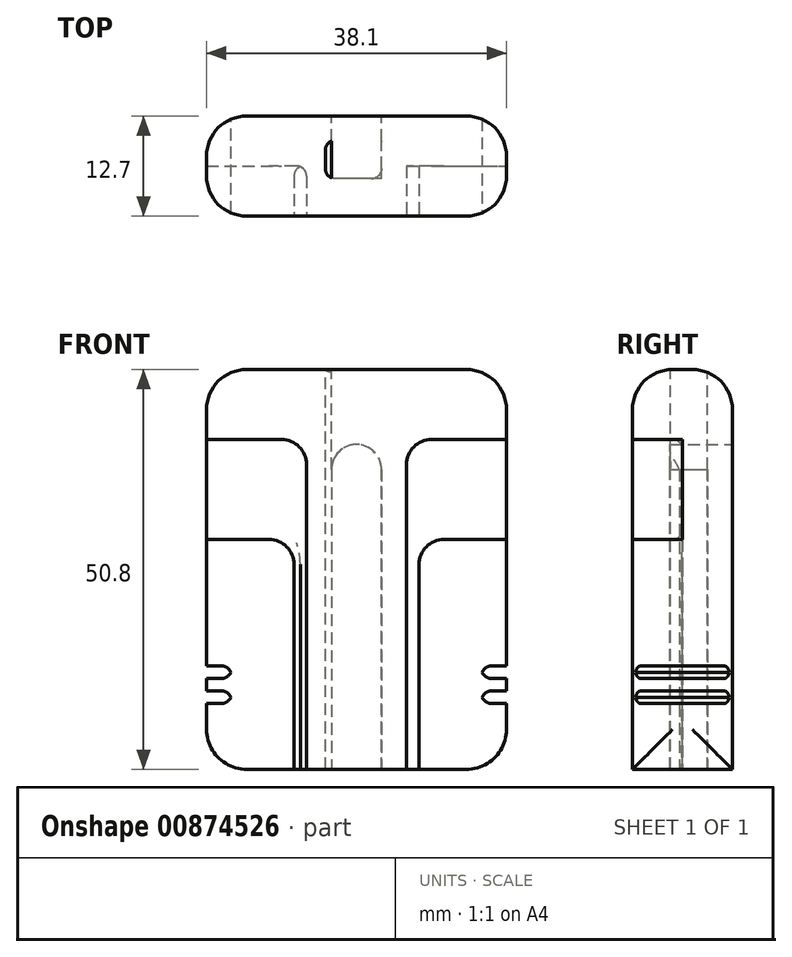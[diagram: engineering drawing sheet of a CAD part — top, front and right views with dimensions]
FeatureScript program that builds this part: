
annotation { "Feature Type Name" : "Feature", "Feature Type Description" : "" }
export const myFeature = defineFeature(function(context is Context, id is Id, definition is map)
    precondition{}
    {
        {
            var Q0;
            Q0=qCreatedBy(makeId("Front.planeOp"),FACE);
            var sketch = newSketch(context, id + "F0", { "sketchPlane" : qUnion([Q0])});
            skLineSegment(sketch, "E0.bottom", {"start": v(0, 50.8) * mm, "end": v(38.1, 50.8) * mm});
            skLineSegment(sketch, "E0.top", {"start": v(0, 0) * mm, "end": v(38.1, 0) * mm});
            skLineSegment(sketch, "E0.left", {"start": v(0, 50.8) * mm, "end": v(0, 0) * mm});
            skLineSegment(sketch, "E0.right", {"start": v(38.1, 50.8) * mm, "end": v(38.1, 0) * mm});
            skSolve(sketch);
        }
        {
            var Q0;
            Q0 = qSketchRegion(id + "F0", true);
            extrude(context, id + "F1", {"entities" : qUnion([Q0]), "depth" : 12.7 * mm, "offsetDistance" : 25.4 * mm});
        }
        {
            var Q0;
            Q0=makeQuery(id+"F1.opExtrude","CAP_FACE",FACE,{"disambiguationData":[OSD([sQuery(id+"F0.wireOp",EDGE,"E0.bottom"),sQuery(id+"F0.wireOp",EDGE,"E0.top"),sQuery(id+"F0.wireOp",EDGE,"E0.left"),sQuery(id+"F0.wireOp",EDGE,"E0.right")])],"isStart":false});
            var sketch = newSketch(context, id + "F2", { "sketchPlane" : qUnion([Q0])});
            skLineSegment(sketch, "E1.bottom", {"start": v(0, 41.91) * mm, "end": v(9.52, 41.91) * mm});
            skLineSegment(sketch, "E1.top", {"start": v(0, 29.21) * mm, "end": v(7.94, 29.21) * mm});
            skLineSegment(sketch, "E1.left", {"start": v(0, 41.91) * mm, "end": v(0, 29.21) * mm});
            skLineSegment(sketch, "E1.right", {"start": v(38.1, 41.91) * mm, "end": v(38.1, 29.21) * mm});
            skLineSegment(sketch, "E2.top", {"start": v(11.11, 0) * mm, "end": v(12.7, 0) * mm});
            skLineSegment(sketch, "E2.left", {"start": v(11.11, 26.04) * mm, "end": v(11.11, 0) * mm});
            skLineSegment(sketch, "E2.right", {"start": v(12.7, 29.21) * mm, "end": v(12.7, 0) * mm});
            skLineSegment(sketch, "E3.top", {"start": v(25.4, 0) * mm, "end": v(26.99, 0) * mm});
            skLineSegment(sketch, "E3.left", {"start": v(25.4, 29.2) * mm, "end": v(25.4, 0) * mm});
            skLineSegment(sketch, "E3.right", {"start": v(26.99, 26.03) * mm, "end": v(26.99, 0) * mm});
            skLineSegment(sketch, "E4.left", {"start": v(12.7, 29.21) * mm, "end": v(12.7, 38.74) * mm});
            skLineSegment(sketch, "E4.right", {"start": v(25.4, 29.24) * mm, "end": v(25.4, 38.73) * mm});
            skLineSegment(sketch, "E5.trimOffspring", {"start": v(30.16, 29.21) * mm, "end": v(38.1, 29.21) * mm});
            skLineSegment(sketch, "E6.trimOffspring", {"start": v(28.58, 41.91) * mm, "end": v(38.1, 41.91) * mm});
            skPoint(sketch, "E7.visualSharp", {"position": v(11.11, 29.21) * mm});
            skArc(sketch, "E7.filletArc", {"start": v(11.11, 26.04) * mm, "mid": v(10.18, 28.28) * mm, "end": v(7.94, 29.21) * mm});
            skPoint(sketch, "E8.visualSharp", {"position": v(12.7, 41.91) * mm});
            skArc(sketch, "E8.filletArc", {"start": v(12.7, 38.74) * mm, "mid": v(11.77, 40.98) * mm, "end": v(9.52, 41.91) * mm});
            skPoint(sketch, "E9.visualSharp", {"position": v(25.4, 41.9) * mm});
            skArc(sketch, "E9.filletArc", {"start": v(28.58, 41.9) * mm, "mid": v(26.33, 40.98) * mm, "end": v(25.4, 38.73) * mm});
            skPoint(sketch, "E10.visualSharp", {"position": v(26.99, 29.2) * mm});
            skArc(sketch, "E10.filletArc", {"start": v(30.16, 29.2) * mm, "mid": v(27.92, 28.28) * mm, "end": v(26.99, 26.03) * mm});
            skLineSegment(sketch, "E11.bottom", {"start": v(0, 9.97) * mm, "end": v(3.18, 9.97) * mm});
            skLineSegment(sketch, "E11.top", {"start": v(0, 8.38) * mm, "end": v(3.18, 8.38) * mm});
            skLineSegment(sketch, "E11.left", {"start": v(0, 9.97) * mm, "end": v(0, 8.38) * mm});
            skLineSegment(sketch, "E11.right", {"start": v(3.18, 9.97) * mm, "end": v(3.18, 8.38) * mm});
            skLineSegment(sketch, "E12.bottom", {"start": v(38.1, 9.97) * mm, "end": v(34.93, 9.97) * mm});
            skLineSegment(sketch, "E12.top", {"start": v(38.1, 8.38) * mm, "end": v(34.93, 8.38) * mm});
            skLineSegment(sketch, "E12.left", {"start": v(38.1, 9.97) * mm, "end": v(38.1, 8.38) * mm});
            skLineSegment(sketch, "E12.right", {"start": v(34.93, 9.97) * mm, "end": v(34.93, 8.38) * mm});
            skLineSegment(sketch, "E13", {"start": v(19.05, 0) * mm, "end": v(19.05, 50.8) * mm});
            skArc(sketch, "E14.MirrorCS", {"start": v(25.4, 38.74) * mm, "mid": v(26.33, 40.98) * mm, "end": v(28.58, 41.91) * mm});
            skLineSegment(sketch, "E15.MirrorCS", {"start": v(38.1, 41.91) * mm, "end": v(28.58, 41.91) * mm});
            skLineSegment(sketch, "E16.MirrorCS", {"start": v(38.1, 29.21) * mm, "end": v(30.16, 29.21) * mm});
            skArc(sketch, "E17.MirrorCS", {"start": v(26.99, 26.04) * mm, "mid": v(27.92, 28.28) * mm, "end": v(30.16, 29.21) * mm});
            skLineSegment(sketch, "E18.MirrorCS", {"start": v(26.99, 26.04) * mm, "end": v(26.99, 0) * mm});
            skLineSegment(sketch, "E19.MirrorCS", {"start": v(25.4, 29.21) * mm, "end": v(25.4, 0) * mm});
            skLineSegment(sketch, "E20.MirrorCS", {"start": v(25.4, 29.21) * mm, "end": v(25.4, 38.74) * mm});
            skLineSegment(sketch, "E21.bottom", {"start": v(3.18, 9.97) * mm, "end": v(0, 9.97) * mm});
            skLineSegment(sketch, "E21.top", {"start": v(3.18, 10.76) * mm, "end": v(0, 10.76) * mm});
            skLineSegment(sketch, "E21.left", {"start": v(3.18, 9.97) * mm, "end": v(3.18, 10.76) * mm});
            skLineSegment(sketch, "E21.right", {"start": v(0, 9.97) * mm, "end": v(0, 10.76) * mm});
            skLineSegment(sketch, "E22.bottom", {"start": v(34.93, 9.97) * mm, "end": v(38.1, 9.97) * mm});
            skLineSegment(sketch, "E22.top", {"start": v(34.93, 10.76) * mm, "end": v(38.1, 10.76) * mm});
            skLineSegment(sketch, "E22.left", {"start": v(34.93, 9.97) * mm, "end": v(34.93, 10.76) * mm});
            skLineSegment(sketch, "E22.right", {"start": v(38.1, 9.97) * mm, "end": v(38.1, 10.76) * mm});
            skLineSegment(sketch, "E23.MirrorCS", {"start": v(3.18, 11.56) * mm, "end": v(3.18, 13.14) * mm});
            skLineSegment(sketch, "E24.MirrorCS", {"start": v(0, 11.56) * mm, "end": v(3.18, 11.56) * mm});
            skLineSegment(sketch, "E25.MirrorCS", {"start": v(0, 13.14) * mm, "end": v(3.18, 13.14) * mm});
            skLineSegment(sketch, "E26.MirrorCS", {"start": v(34.93, 11.56) * mm, "end": v(34.93, 13.14) * mm});
            skLineSegment(sketch, "E27.MirrorCS", {"start": v(38.1, 13.14) * mm, "end": v(34.93, 13.14) * mm});
            skLineSegment(sketch, "E28.MirrorCS", {"start": v(38.1, 11.56) * mm, "end": v(34.93, 11.56) * mm});
            skSolve(sketch);
        }
        {
            var Q0;
            Q0=makeQuery(id+"F2.imprint","IMPRINT",FACE,{"disambiguationData":[TD([[makeQuery(id+"F2.imprint","IMPRINT",EDGE,{"derivedFrom":sQuery(id+"F2.wireOp",EDGE,"E1.bottom")}),-1.0]])]});
            var Q1;
            Q1=makeQuery(id+"F2.imprint","IMPRINT",FACE,{"disambiguationData":[TD([[makeQuery(id+"F2.imprint","IMPRINT",EDGE,{"derivedFrom":sQuery(id+"F2.wireOp",EDGE,"E1.right")}),-1.0]])]});
            extrude(context, id + "F3", {"entities" : qUnion([Q0, Q1]), "operationType" : NewBodyOperationType.REMOVE, "oppositeDirection" : true, "depth" : 6.35 * mm, "offsetDistance" : 25.4 * mm});
        }
        {
            var Q0;
            Q0=makeQuery(id+"F2.imprint","IMPRINT",FACE,{"disambiguationData":[TD([[makeQuery(id+"F2.imprint","IMPRINT",EDGE,{"derivedFrom":sQuery(id+"F2.wireOp",EDGE,"E23.MirrorCS")}),1.0]])]});
            var Q1;
            Q1=makeQuery(id+"F2.imprint","IMPRINT",FACE,{"disambiguationData":[TD([[makeQuery(id+"F2.imprint","IMPRINT",EDGE,{"derivedFrom":sQuery(id+"F2.wireOp",EDGE,"E26.MirrorCS")}),-1.0]])]});
            var Q2;
            Q2=makeQuery(id+"F2.imprint","IMPRINT",FACE,{"disambiguationData":[TD([[makeQuery(id+"F2.imprint","IMPRINT",EDGE,{"derivedFrom":sQuery(id+"F2.wireOp",EDGE,"E12.top")}),-1.0]])]});
            var Q3;
            Q3=makeQuery(id+"F2.imprint","IMPRINT",FACE,{"disambiguationData":[TD([[makeQuery(id+"F2.imprint","IMPRINT",EDGE,{"derivedFrom":sQuery(id+"F2.wireOp",EDGE,"E11.top")}),1.0]])]});
            extrude(context, id + "F4", {"entities" : qUnion([Q0, Q1, Q2, Q3]), "operationType" : NewBodyOperationType.REMOVE, "endBound" : BoundingType.THROUGH_ALL, "oppositeDirection" : true, "depth" : 6.35 * mm, "offsetDistance" : 25.4 * mm});
        }
        {
            var Q0;
            Q0=makeQuery(id+"F2.imprint","IMPRINT",FACE,{"disambiguationData":[TD([[makeQuery(id+"F2.imprint","IMPRINT",EDGE,{"derivedFrom":sQuery(id+"F2.wireOp",EDGE,"E1.right")}),-1.0]])]});
            extrude(context, id + "F5", {"entities" : qUnion([Q0]), "operationType" : NewBodyOperationType.REMOVE, "oppositeDirection" : true, "depth" : 6.35 * mm, "offsetDistance" : 25.4 * mm});
        }
        {
            var Q0;
            Q0=makeQuery(id+"F3.boolean.opBoolean","COPY",EDGE,{"derivedFrom":makeQuery(id+"F3.opExtrude","CAP_EDGE",EDGE,{"disambiguationData":[OSD([sQuery(id+"F2.wireOp",EDGE,"E1.bottom")])],"isStart":false})});
            var Q1;
            Q1=makeQuery(id+"F3.boolean.opBoolean","COPY",EDGE,{"derivedFrom":makeQuery(id+"F3.opExtrude","CAP_EDGE",EDGE,{"disambiguationData":[OSD([sQuery(id+"F2.wireOp",EDGE,"E15.MirrorCS")])],"isStart":false})});
            var Q2;
            Q2=makeQuery(id+"F3.boolean.opBoolean","COPY",EDGE,{"derivedFrom":makeQuery(id+"F3.opExtrude","CAP_EDGE",EDGE,{"disambiguationData":[OSD([sQuery(id+"F2.wireOp",EDGE,"E16.MirrorCS")])],"isStart":false})});
            var Q3;
            Q3=makeQuery(id+"F3.boolean.opBoolean","COPY",EDGE,{"derivedFrom":makeQuery(id+"F3.opExtrude","CAP_EDGE",EDGE,{"disambiguationData":[OSD([sQuery(id+"F2.wireOp",EDGE,"E1.top")])],"isStart":false})});
            var Q4;
            Q4=makeQuery(id+"F4.boolean.opBoolean","COPY",EDGE,{"derivedFrom":makeQuery(id+"F4.opExtrude","SWEPT_EDGE",EDGE,{"disambiguationData":[OSD([sQuery(id+"F2.wireOp",EDGE,"E26.MirrorCS"),sQuery(id+"F2.wireOp",EDGE,"E28.MirrorCS")])]})});
            var Q5;
            Q5=makeQuery(id+"F4.boolean.opBoolean","COPY",EDGE,{"derivedFrom":makeQuery(id+"F4.opExtrude","SWEPT_EDGE",EDGE,{"disambiguationData":[OSD([sQuery(id+"F2.wireOp",EDGE,"E12.top"),sQuery(id+"F2.wireOp",EDGE,"E12.right")])]})});
            var Q6;
            Q6=makeQuery(id+"F4.boolean.opBoolean","COPY",EDGE,{"derivedFrom":makeQuery(id+"F4.opExtrude","SWEPT_EDGE",EDGE,{"disambiguationData":[OSD([sQuery(id+"F2.wireOp",EDGE,"E26.MirrorCS"),sQuery(id+"F2.wireOp",EDGE,"E27.MirrorCS")])]})});
            var Q7;
            Q7=makeQuery(id+"F4.boolean.opBoolean","COPY",EDGE,{"derivedFrom":makeQuery(id+"F4.opExtrude","SWEPT_EDGE",EDGE,{"disambiguationData":[OSD([sQuery(id+"F2.wireOp",EDGE,"E12.right"),sQuery(id+"F2.wireOp",EDGE,"E22.bottom"),sQuery(id+"F2.wireOp",EDGE,"E22.left")])]})});
            var Q8;
            Q8=makeQuery(id+"F4.boolean.opBoolean","COPY",EDGE,{"derivedFrom":makeQuery(id+"F4.opExtrude","SWEPT_EDGE",EDGE,{"disambiguationData":[OSD([sQuery(id+"F2.wireOp",EDGE,"E11.top"),sQuery(id+"F2.wireOp",EDGE,"E11.right")])]})});
            var Q9;
            Q9=makeQuery(id+"F4.boolean.opBoolean","COPY",EDGE,{"derivedFrom":makeQuery(id+"F4.opExtrude","SWEPT_EDGE",EDGE,{"disambiguationData":[OSD([sQuery(id+"F2.wireOp",EDGE,"E23.MirrorCS"),sQuery(id+"F2.wireOp",EDGE,"E24.MirrorCS")])]})});
            var Q10;
            Q10=makeQuery(id+"F4.boolean.opBoolean","COPY",EDGE,{"derivedFrom":makeQuery(id+"F4.opExtrude","SWEPT_EDGE",EDGE,{"disambiguationData":[OSD([sQuery(id+"F2.wireOp",EDGE,"E11.right"),sQuery(id+"F2.wireOp",EDGE,"E21.bottom"),sQuery(id+"F2.wireOp",EDGE,"E21.left")])]})});
            var Q11;
            Q11=makeQuery(id+"F4.boolean.opBoolean","COPY",EDGE,{"derivedFrom":makeQuery(id+"F4.opExtrude","SWEPT_EDGE",EDGE,{"disambiguationData":[OSD([sQuery(id+"F2.wireOp",EDGE,"E23.MirrorCS"),sQuery(id+"F2.wireOp",EDGE,"E25.MirrorCS")])]})});
            fillet(context, id + "F6", {"entities" : qUnion([Q0, Q1, Q2, Q3, Q4, Q5, Q6, Q7, Q8, Q9, Q10, Q11]), "radius" : 1.27 * mm, "tangentPropagation" : true, "allowEdgeOverflow" : false});
        }
        {
            var Q0;
            Q0=qCreatedBy(makeId("Front.planeOp"),FACE);
            var sketch = newSketch(context, id + "F7", { "sketchPlane" : qUnion([Q0])});
            skLineSegment(sketch, "E29.bottom", {"start": v(19.05, 41.28) * mm, "end": v(19.05, 41.28) * mm});
            skLineSegment(sketch, "E29.top", {"start": v(22.23, 0) * mm, "end": v(15.88, 0) * mm});
            skLineSegment(sketch, "E29.left", {"start": v(22.23, 38.1) * mm, "end": v(22.22, 0) * mm});
            skLineSegment(sketch, "E29.right", {"start": v(15.88, 38.1) * mm, "end": v(15.88, 0) * mm});
            skPoint(sketch, "E30", {"position": v(19.05, 0) * mm});
            skPoint(sketch, "E31.visualSharp", {"position": v(15.88, 41.28) * mm});
            skArc(sketch, "E31.filletArc", {"start": v(19.05, 41.28) * mm, "mid": v(16.8, 40.35) * mm, "end": v(15.88, 38.1) * mm});
            skLineSegment(sketch, "E32.0", {"start": v(15.08, 38.1) * mm, "end": v(15.08, 0) * mm});
            skPoint(sketch, "E33.visualSharp", {"position": v(22.23, 41.28) * mm});
            skArc(sketch, "E33.filletArc", {"start": v(22.23, 38.1) * mm, "mid": v(21.3, 40.35) * mm, "end": v(19.05, 41.28) * mm});
            skLineSegment(sketch, "E34.0", {"start": v(23.02, 38.1) * mm, "end": v(23.02, 0) * mm});
            skArc(sketch, "E35.0", {"start": v(19.05, 42.07) * mm, "mid": v(16.24, 40.9) * mm, "end": v(15.08, 38.1) * mm});
            skArc(sketch, "E35.1", {"start": v(23.02, 38.1) * mm, "mid": v(21.86, 40.9) * mm, "end": v(19.05, 42.07) * mm});
            skSolve(sketch);
        }
        {
            var Q0;
            Q0=makeQuery(id+"F7.imprint","IMPRINT",FACE,{"disambiguationData":[TD([[makeQuery(id+"F7.imprint","IMPRINT",EDGE,{"derivedFrom":sQuery(id+"F7.wireOp",EDGE,"E29.top")}),-1.0]])]});
            extrude(context, id + "F8", {"entities" : qUnion([Q0]), "operationType" : NewBodyOperationType.REMOVE, "depth" : 7.94 * mm, "offsetDistance" : 25.4 * mm});
        }
        {
            var Q0;
            Q0=makeQuery(id+"F8.boolean.opBoolean","COPY",FACE,{"derivedFrom":makeQuery(id+"F8.opExtrude","SWEPT_FACE",FACE,{"disambiguationData":[OSD([sQuery(id+"F7.wireOp",EDGE,"E29.left")])]})});
            var sketch = newSketch(context, id + "F9", { "sketchPlane" : qUnion([Q0])});
            skLineSegment(sketch, "E36.bottom", {"start": v(7.94, 38.1) * mm, "end": v(3.18, 38.1) * mm});
            skLineSegment(sketch, "E36.top", {"start": v(7.94, 0) * mm, "end": v(3.18, 0) * mm});
            skLineSegment(sketch, "E36.left", {"start": v(7.94, 38.1) * mm, "end": v(7.94, 0) * mm});
            skLineSegment(sketch, "E36.right", {"start": v(3.17, 38.1) * mm, "end": v(3.18, 0) * mm});
            skSolve(sketch);
        }
        {
            var Q0;
            Q0 = qSketchRegion(id + "F9", true);
            extrude(context, id + "F10", {"entities" : qUnion([Q0]), "operationType" : NewBodyOperationType.REMOVE, "oppositeDirection" : true, "depth" : 1 / 812.8 * mm, "offsetDistance" : 25.4 * mm});
        }
        {
            var Q0;
            Q0=makeQuery(id+"F8.boolean.opBoolean","COPY",FACE,{"derivedFrom":makeQuery(id+"F8.opExtrude","SWEPT_FACE",FACE,{"disambiguationData":[OSD([sQuery(id+"F7.wireOp",EDGE,"E29.right")])]})});
            var sketch = newSketch(context, id + "F11", { "sketchPlane" : qUnion([Q0])});
            skLineSegment(sketch, "E37.bottom", {"start": v(-7.94, 0) * mm, "end": v(-3.17, 0) * mm});
            skLineSegment(sketch, "E37.top", {"start": v(-7.94, 57.15) * mm, "end": v(-3.18, 57.15) * mm});
            skLineSegment(sketch, "E37.left", {"start": v(-7.94, 0) * mm, "end": v(-7.94, 57.15) * mm});
            skLineSegment(sketch, "E37.right", {"start": v(-3.17, 0) * mm, "end": v(-3.18, 57.15) * mm});
            skSolve(sketch);
        }
        {
            var Q0;
            Q0 = qSketchRegion(id + "F11", true);
            extrude(context, id + "F12", {"entities" : qUnion([Q0]), "operationType" : NewBodyOperationType.REMOVE, "oppositeDirection" : true, "depth" : 0.8 * mm, "offsetDistance" : 25.4 * mm});
        }
        {
            var Q0;
            Q0=makeQuery(id+"F10.boolean.opBoolean","COPY",EDGE,{"derivedFrom":makeQuery(id+"F10.opExtrude","CAP_EDGE",EDGE,{"disambiguationData":[OSD([sQuery(id+"F9.wireOp",EDGE,"E36.left")])],"isStart":false})});
            var Q1;
            Q1=makeQuery(id+"F12.boolean.opBoolean","COPY",EDGE,{"derivedFrom":makeQuery(id+"F12.opExtrude","CAP_EDGE",EDGE,{"disambiguationData":[OSD([sQuery(id+"F11.wireOp",EDGE,"E37.left")])],"isStart":false})});
            var Q2;
            Q2=makeQuery(id+"F12.boolean.opBoolean","COPY",EDGE,{"derivedFrom":makeQuery(id+"F12.opExtrude","CAP_EDGE",EDGE,{"disambiguationData":[OSD([sQuery(id+"F11.wireOp",EDGE,"E37.right")])],"isStart":false})});
            var Q3;
            Q3=makeQuery(id+"F10.boolean.opBoolean","COPY",EDGE,{"derivedFrom":makeQuery(id+"F10.opExtrude","CAP_EDGE",EDGE,{"disambiguationData":[OSD([sQuery(id+"F9.wireOp",EDGE,"E36.right")])],"isStart":false})});
            var Q4;
            Q4=makeQuery(id+"F8.boolean.opBoolean","COPY",EDGE,{"derivedFrom":makeQuery(id+"F8.opExtrude","CAP_EDGE",EDGE,{"disambiguationData":[OSD([sQuery(id+"F7.wireOp",EDGE,"E29.left")])],"isStart":true})});
            fillet(context, id + "F13", {"entities" : qUnion([Q0, Q1, Q2, Q3, Q4]), "radius" : 1.27 * mm, "tangentPropagation" : true, "allowEdgeOverflow" : false});
        }
        {
            var Q0;
            {var subQ0=sQuery(id+"F0.wireOp",EDGE,"E0.bottom");var subQ1=sQuery(id+"F0.wireOp",EDGE,"E0.right");Q0=makeQuery(id+"F3.boolean.opBoolean","SPLIT",EDGE,{"disambiguationData":[TD([makeQuery(id+"F1.opExtrude","SWEPT_FACE",FACE,{"disambiguationData":[OSD([subQ0])]})])],"derivedFrom":makeQuery(id+"F1.opExtrude","CAP_EDGE",EDGE,{"disambiguationData":[OSD([subQ1])],"isStart":true})});}
            var Q1;
            Q1=makeQuery(id+"F1.opExtrude","CAP_EDGE",EDGE,{"disambiguationData":[OSD([sQuery(id+"F0.wireOp",EDGE,"E0.bottom")])],"isStart":true});
            var Q2;
            {var subQ0=sQuery(id+"F0.wireOp",EDGE,"E0.bottom");var subQ1=sQuery(id+"F0.wireOp",EDGE,"E0.left");Q2=makeQuery(id+"F3.boolean.opBoolean","SPLIT",EDGE,{"disambiguationData":[TD([makeQuery(id+"F1.opExtrude","SWEPT_FACE",FACE,{"disambiguationData":[OSD([subQ0])]})])],"derivedFrom":makeQuery(id+"F1.opExtrude","CAP_EDGE",EDGE,{"disambiguationData":[OSD([subQ1])],"isStart":true})});}
            var Q3;
            {var subQ0=sQuery(id+"F0.wireOp",EDGE,"E0.right");var subQ1=sQuery(id+"F0.wireOp",EDGE,"E0.top");Q3=makeQuery(id+"F3.boolean.opBoolean","SPLIT",EDGE,{"disambiguationData":[TD([makeQuery(id+"F1.opExtrude","SWEPT_FACE",FACE,{"disambiguationData":[OSD([subQ1])]})])],"derivedFrom":makeQuery(id+"F1.opExtrude","CAP_EDGE",EDGE,{"disambiguationData":[OSD([subQ0])],"isStart":true})});}
            var Q4;
            Q4=makeQuery(id+"F1.opExtrude","CAP_EDGE",EDGE,{"disambiguationData":[OSD([sQuery(id+"F0.wireOp",EDGE,"E0.bottom")])],"isStart":false});
            var Q5;
            {var subQ0=sQuery(id+"F0.wireOp",EDGE,"E0.right");var subQ1=sQuery(id+"F0.wireOp",EDGE,"E0.bottom");var subQ3=makeQuery(id+"F3.opExtrude","SWEPT_FACE",FACE,{"disambiguationData":[OSD([sQuery(id+"F2.wireOp",EDGE,"E12.bottom")])]});Q5=makeQuery(id+"F5.boolean.opBoolean","SPLIT",EDGE,{"disambiguationData":[TD([makeQuery(id+"F3.boolean.opBoolean","COPY",FACE,{"derivedFrom":subQ3})])],"derivedFrom":makeQuery(id+"F3.boolean.opBoolean","SPLIT",EDGE,{"disambiguationData":[TD([makeQuery(id+"F1.opExtrude","SWEPT_FACE",FACE,{"disambiguationData":[OSD([subQ1])]})])],"derivedFrom":makeQuery(id+"F1.opExtrude","CAP_EDGE",EDGE,{"disambiguationData":[OSD([subQ0])],"isStart":false})})});}
            var Q6;
            {var subQ0=sQuery(id+"F0.wireOp",EDGE,"E0.right");var subQ1=sQuery(id+"F0.wireOp",EDGE,"E0.top");Q6=makeQuery(id+"F3.boolean.opBoolean","SPLIT",EDGE,{"disambiguationData":[TD([makeQuery(id+"F1.opExtrude","SWEPT_FACE",FACE,{"disambiguationData":[OSD([subQ1])]})])],"derivedFrom":makeQuery(id+"F1.opExtrude","CAP_EDGE",EDGE,{"disambiguationData":[OSD([subQ0])],"isStart":false})});}
            var Q7;
            {var subQ0=sQuery(id+"F0.wireOp",EDGE,"E0.left");var subQ1=sQuery(id+"F0.wireOp",EDGE,"E0.bottom");var subQ4=makeQuery(id+"F3.opExtrude","SWEPT_FACE",FACE,{"disambiguationData":[OSD([sQuery(id+"F2.wireOp",EDGE,"E11.bottom")])]});Q7=makeQuery(id+"F4.boolean.opBoolean","SPLIT",EDGE,{"disambiguationData":[TD([makeQuery(id+"F3.boolean.opBoolean","COPY",FACE,{"derivedFrom":subQ4})])],"derivedFrom":makeQuery(id+"F3.boolean.opBoolean","SPLIT",EDGE,{"disambiguationData":[TD([makeQuery(id+"F1.opExtrude","SWEPT_FACE",FACE,{"disambiguationData":[OSD([subQ1])]})])],"derivedFrom":makeQuery(id+"F1.opExtrude","CAP_EDGE",EDGE,{"disambiguationData":[OSD([subQ0])],"isStart":false})})});}
            var Q8;
            Q8=makeQuery(id+"F4.boolean.opBoolean","COPY",EDGE,{"derivedFrom":makeQuery(id+"F4.opExtrude","CAP_EDGE",EDGE,{"disambiguationData":[OSD([sQuery(id+"F2.wireOp",EDGE,"E2.right"),sQuery(id+"F2.wireOp",EDGE,"E4.left")])],"isStart":true})});
            var Q9;
            Q9=makeQuery(id+"F4.boolean.opBoolean","COPY",EDGE,{"derivedFrom":makeQuery(id+"F4.opExtrude","CAP_EDGE",EDGE,{"disambiguationData":[OSD([sQuery(id+"F2.wireOp",EDGE,"E2.left")])],"isStart":true})});
            var Q10;
            Q10=makeQuery(id+"F5.boolean.opBoolean","COPY",EDGE,{"derivedFrom":makeQuery(id+"F5.opExtrude","CAP_EDGE",EDGE,{"disambiguationData":[OSD([sQuery(id+"F2.wireOp",EDGE,"E19.MirrorCS"),sQuery(id+"F2.wireOp",EDGE,"E20.MirrorCS")])],"isStart":true})});
            var Q11;
            Q11=makeQuery(id+"F5.boolean.opBoolean","COPY",EDGE,{"derivedFrom":makeQuery(id+"F5.opExtrude","CAP_EDGE",EDGE,{"disambiguationData":[OSD([sQuery(id+"F2.wireOp",EDGE,"E18.MirrorCS")])],"isStart":true})});
            var Q12;
            {var subQ0=sQuery(id+"F0.wireOp",EDGE,"E0.left");var subQ1=sQuery(id+"F0.wireOp",EDGE,"E0.top");var subQ4=makeQuery(id+"F3.opExtrude","SWEPT_FACE",FACE,{"disambiguationData":[OSD([sQuery(id+"F2.wireOp",EDGE,"E1.top")])]});Q12=makeQuery(id+"F4.boolean.opBoolean","SPLIT",EDGE,{"disambiguationData":[TD([makeQuery(id+"F3.boolean.opBoolean","COPY",FACE,{"derivedFrom":subQ4})])],"derivedFrom":makeQuery(id+"F3.boolean.opBoolean","SPLIT",EDGE,{"disambiguationData":[TD([makeQuery(id+"F1.opExtrude","SWEPT_FACE",FACE,{"disambiguationData":[OSD([subQ1])]})])],"derivedFrom":makeQuery(id+"F1.opExtrude","CAP_EDGE",EDGE,{"disambiguationData":[OSD([subQ0])],"isStart":false})})});}
            var Q13;
            {var subQ0=sQuery(id+"F0.wireOp",EDGE,"E0.left");var subQ1=sQuery(id+"F0.wireOp",EDGE,"E0.top");var subQ3=makeQuery(id+"F1.opExtrude","SWEPT_FACE",FACE,{"disambiguationData":[OSD([subQ1])]});Q13=makeQuery(id+"F4.boolean.opBoolean","SPLIT",EDGE,{"disambiguationData":[TD([subQ3])],"derivedFrom":makeQuery(id+"F3.boolean.opBoolean","SPLIT",EDGE,{"disambiguationData":[TD([subQ3])],"derivedFrom":makeQuery(id+"F1.opExtrude","CAP_EDGE",EDGE,{"disambiguationData":[OSD([subQ0])],"isStart":false})})});}
            var Q14;
            {var subQ0=sQuery(id+"F0.wireOp",EDGE,"E0.right");var subQ1=sQuery(id+"F0.wireOp",EDGE,"E0.top");var subQ3=makeQuery(id+"F1.opExtrude","SWEPT_FACE",FACE,{"disambiguationData":[OSD([subQ1])]});Q14=makeQuery(id+"F4.boolean.opBoolean","SPLIT",EDGE,{"disambiguationData":[TD([subQ3])],"derivedFrom":makeQuery(id+"F3.boolean.opBoolean","SPLIT",EDGE,{"disambiguationData":[TD([subQ3])],"derivedFrom":makeQuery(id+"F1.opExtrude","CAP_EDGE",EDGE,{"disambiguationData":[OSD([subQ0])],"isStart":false})})});}
            var Q15;
            {var subQ0=sQuery(id+"F0.wireOp",EDGE,"E0.right");var subQ1=sQuery(id+"F0.wireOp",EDGE,"E0.top");var subQ4=makeQuery(id+"F3.opExtrude","SWEPT_FACE",FACE,{"disambiguationData":[OSD([sQuery(id+"F2.wireOp",EDGE,"E16.MirrorCS")])]});Q15=makeQuery(id+"F4.boolean.opBoolean","SPLIT",EDGE,{"disambiguationData":[TD([makeQuery(id+"F3.boolean.opBoolean","COPY",FACE,{"derivedFrom":subQ4})])],"derivedFrom":makeQuery(id+"F3.boolean.opBoolean","SPLIT",EDGE,{"disambiguationData":[TD([makeQuery(id+"F1.opExtrude","SWEPT_FACE",FACE,{"disambiguationData":[OSD([subQ1])]})])],"derivedFrom":makeQuery(id+"F1.opExtrude","CAP_EDGE",EDGE,{"disambiguationData":[OSD([subQ0])],"isStart":false})})});}
            var Q16;
            Q16=makeQuery(id+"F1.opExtrude","SWEPT_EDGE",EDGE,{"disambiguationData":[OSD([sQuery(id+"F0.wireOp",EDGE,"E0.bottom"),sQuery(id+"F0.wireOp",EDGE,"E0.right")])]});
            var Q17;
            Q17=makeQuery(id+"F1.opExtrude","SWEPT_EDGE",EDGE,{"disambiguationData":[OSD([sQuery(id+"F0.wireOp",EDGE,"E0.bottom"),sQuery(id+"F0.wireOp",EDGE,"E0.left")])]});
            var Q18;
            Q18=makeQuery(id+"F1.opExtrude","SWEPT_EDGE",EDGE,{"disambiguationData":[OSD([sQuery(id+"F0.wireOp",EDGE,"E0.top"),sQuery(id+"F0.wireOp",EDGE,"E0.left")])]});
            var Q19;
            Q19=makeQuery(id+"F1.opExtrude","SWEPT_EDGE",EDGE,{"disambiguationData":[OSD([sQuery(id+"F0.wireOp",EDGE,"E0.top"),sQuery(id+"F0.wireOp",EDGE,"E0.right")])]});
            fillet(context, id + "F14", {"entities" : qUnion([Q0, Q1, Q2, Q3, Q4, Q5, Q6, Q7, Q8, Q9, Q10, Q11, Q12, Q13, Q14, Q15, Q16, Q17, Q18, Q19]), "radius" : 5.08 * mm, "tangentPropagation" : true, "allowEdgeOverflow" : false});
        }
    });
